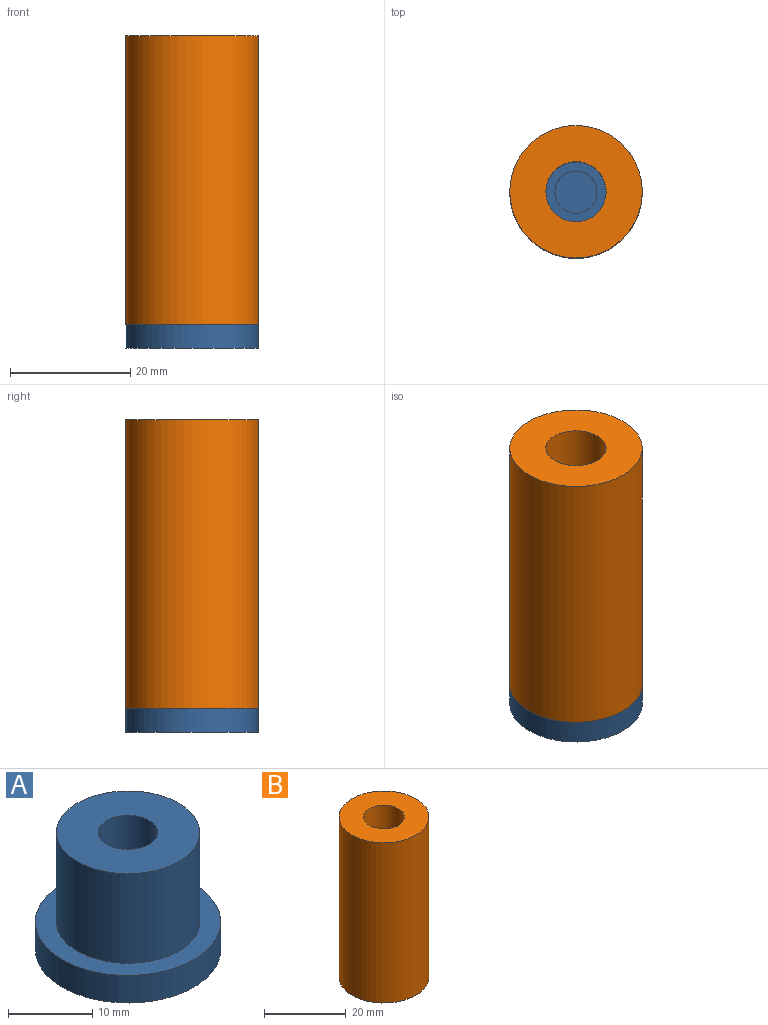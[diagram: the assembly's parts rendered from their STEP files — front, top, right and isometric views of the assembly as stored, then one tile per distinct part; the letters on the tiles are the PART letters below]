
ASSEMBLY  parts=2 mates=1
PART A: 7 faces, bbox 22x22x17 mm
  f0: plane 7x7mm, normal (0,0,1), area 38.5mm2, adj f1
  f1: cylinder r=3.5mm len=13mm, axis (0,0,1), area 285.9mm2, adj f0,f2
  f2: plane 17x17mm, normal (0,0,1), area 188.5mm2, adj f1,f3
  f3: cylinder r=8.5mm len=17mm, axis (0,0,1), area 694.3mm2, adj f2,f4
  f4: plane 22x22mm, normal (0,0,1), area 153.2mm2, adj f3,f5
  f5: cylinder r=11mm len=22mm, axis (0,0,1), area 276.5mm2, adj f4,f6
  f6: plane 22x22mm, normal (0,0,-1), area 380.1mm2, adj f5
PART B: 6 faces, bbox 22x22x48 mm
  f0: plane 22x22mm, normal (0,0,1), area 301.6mm2, adj f1,f5
  f1: cylinder r=11mm len=48mm, axis (0,0,-1), area 3317.5mm2, adj f0,f2
  f2: plane 22x22mm, normal (0,0,-1), area 153.2mm2, adj f1,f3
  f3: cylinder r=8.5mm len=17mm, axis (0,0,-1), area 694.3mm2, adj f2,f4
  f4: plane 17x17mm, normal (0,0,-1), area 148.4mm2, adj f3,f5
  f5: cylinder r=5mm len=35mm, axis (0,0,-1), area 1099.6mm2, adj f0,f4
PLACE A t=(-36.35,-12.37,-0.08)mm
PLACE B t=(-36.35,-12.37,12.92)mm
MATE planar A.f1 <-> B.f1  axis (0,0,1) through (-36.35,-12.37,12.92)mm
